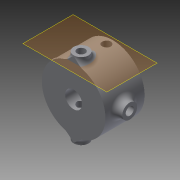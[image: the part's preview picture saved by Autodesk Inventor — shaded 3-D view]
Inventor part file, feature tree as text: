
AUTODESK INVENTOR PART (.ipt)
format: ipt  version: 2014 (Build 180170000, 170)  size: 387,584 bytes
history: native  units: mm
features: extrude x10, sketch x10, fillet x3, other x2
ambient origin geometry x8: Origin, YZ Plane, XZ Plane, XY Plane, X Axis, Y Axis, Z Axis, Center Point
bodies: Body1 (feature_tree)
feature tree (25):
  other  "ソリッド1"
  extrude  "押し出し1"  Depth=30.0mm
  extrude  "押し出し3"  Depth=10.0mm
  extrude  "押し出し4"  Depth=3.8mm
  extrude  "押し出し5"  Depth=30.0mm TaperAngle=360.0deg
  extrude  "押し出し6"  Depth=8.5mm TaperAngle=0.0deg
  extrude  "押し出し7"  Depth=10.0mm TaperAngle=0.0deg
  fillet  "フィレット1"  Radius=7.0mm
  extrude  "押し出し9"  Depth=1.5mm
  extrude  "押し出し10"  TaperAngle=0.0deg  [1 undecoded]
  fillet  "フィレット3"  Radius=36.0mm
  extrude  "押し出し11"  Depth=3.8mm
  other  "作業平面1"
  extrude  "押し出し12"  Depth=40.0mm TaperAngle=0.0deg
  fillet  "フィレット4"  Radius=7.0mm
  sketch  "スケッチ1"
  sketch  "スケッチ3"
  sketch  "スケッチ4"
  sketch  "スケッチ5"
  sketch  "スケッチ6"
  sketch  "スケッチ7"
  sketch  "スケッチ10"
  sketch  "スケッチ11"
  sketch  "スケッチ13"
  sketch  "スケッチ14"
note: 1 required parameter value undecoded (feature->parameter linkage not recoverable at this tier; creation-order binding heuristic only, values carry confidence <= 0.55)
